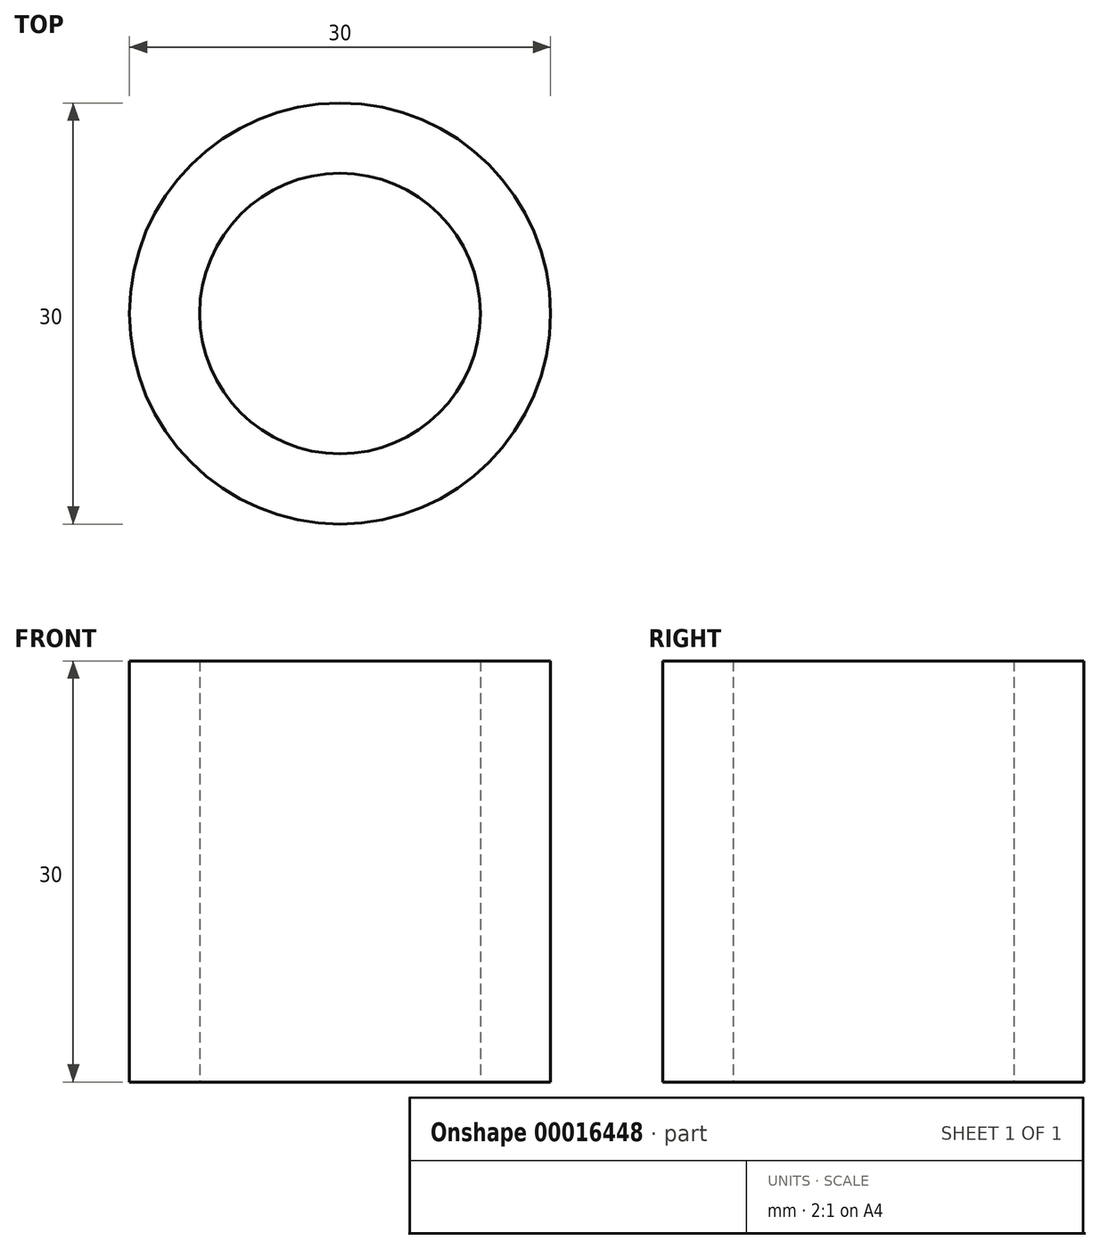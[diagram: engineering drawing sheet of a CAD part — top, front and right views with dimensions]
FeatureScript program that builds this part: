
annotation { "Feature Type Name" : "Feature", "Feature Type Description" : "" }
export const myFeature = defineFeature(function(context is Context, id is Id, definition is map)
    precondition{}
    {
        {
            var Q0;
            Q0=qCreatedBy(makeId("Top.planeOp"),FACE);
            var sketch = newSketch(context, id + "F0", { "sketchPlane" : qUnion([Q0])});
            skCircle(sketch, "E0", {"center": v(0, 0) * mm, "radius": 15 * mm});
            skCircle(sketch, "E1", {"center": v(0, 0) * mm, "radius": 10 * mm});
            skSolve(sketch);
        }
        {
            var Q0;
            Q0=makeQuery(id+"F0.imprint","IMPRINT",FACE,{"disambiguationData":[TD([[makeQuery(id+"F0.imprint","IMPRINT",EDGE,{"derivedFrom":sQuery(id+"F0.wireOp",EDGE,"E0")}),1.0]])]});
            extrude(context, id + "F1", {"entities" : qUnion([Q0]), "depth" : 30 * mm});
        }
    });
